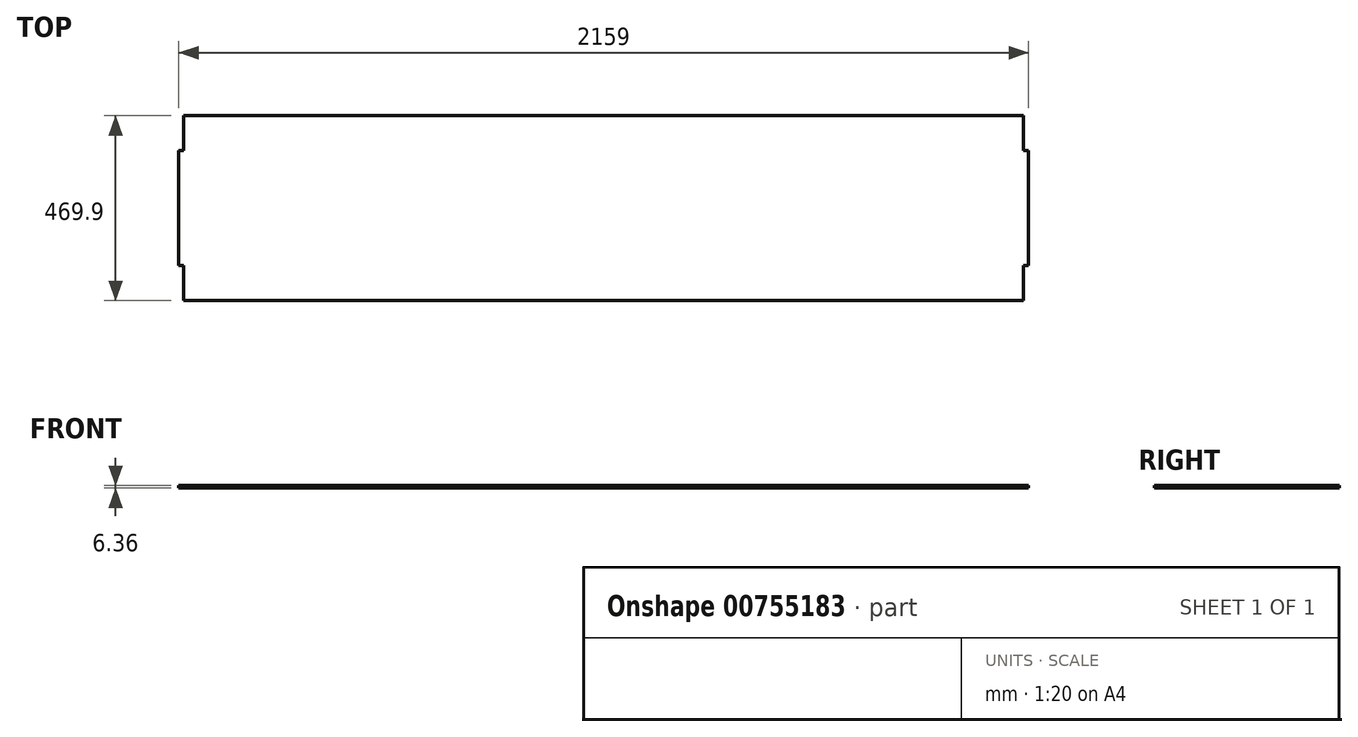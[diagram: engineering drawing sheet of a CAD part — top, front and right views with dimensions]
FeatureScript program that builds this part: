
annotation { "Feature Type Name" : "Feature", "Feature Type Description" : "" }
export const myFeature = defineFeature(function(context is Context, id is Id, definition is map)
    precondition{}
    {
        {
            var Q0;
            Q0=qCreatedBy(makeId("Top.planeOp"),FACE);
            var sketch = newSketch(context, id + "F0", { "sketchPlane" : qUnion([Q0])});
            skLineSegment(sketch, "E0.bottom", {"start": v(-1079.5, 234.95) * mm, "end": v(1079.5, 234.95) * mm});
            skLineSegment(sketch, "E0.top", {"start": v(-1079.5, -234.95) * mm, "end": v(1079.5, -234.95) * mm});
            skLineSegment(sketch, "E0.left", {"start": v(-1079.5, 234.95) * mm, "end": v(-1079.5, -234.95) * mm});
            skLineSegment(sketch, "E0.right", {"start": v(1079.5, 234.95) * mm, "end": v(1079.5, -234.95) * mm});
            skPoint(sketch, "E0.middle", {"position": v(0, 0) * mm});
            skSolve(sketch);
        }
        {
            var Q0;
            Q0 = qSketchRegion(id + "F0", true);
            extrude(context, id + "F1", {"entities" : qUnion([Q0]), "endBound" : BoundingType.SYMMETRIC, "depth" : 6.35 * mm, "offsetDistance" : 25.4 * mm});
        }
        {
            var Q0;
            Q0=makeQuery(id+"F1.opExtrude","CAP_FACE",FACE,{"disambiguationData":[OSD([sQuery(id+"F0.wireOp",EDGE,"E0.bottom"),sQuery(id+"F0.wireOp",EDGE,"E0.top"),sQuery(id+"F0.wireOp",EDGE,"E0.left"),sQuery(id+"F0.wireOp",EDGE,"E0.right")])],"isStart":false});
            var sketch = newSketch(context, id + "F2", { "sketchPlane" : qUnion([Q0])});
            skLineSegment(sketch, "E1", {"start": v(-1079.5, 0) * mm, "end": v(1079.5, 0) * mm, "construction": true});
            skLineSegment(sketch, "E2.bottom", {"start": v(-1079.5, 234.95) * mm, "end": v(-1066.8, 234.95) * mm});
            skLineSegment(sketch, "E2.top", {"start": v(-1079.5, 146.05) * mm, "end": v(-1066.8, 146.05) * mm});
            skLineSegment(sketch, "E2.left", {"start": v(-1079.5, 234.95) * mm, "end": v(-1079.5, 146.05) * mm});
            skLineSegment(sketch, "E2.right", {"start": v(-1066.8, 234.95) * mm, "end": v(-1066.8, 146.05) * mm});
            skLineSegment(sketch, "E3", {"start": v(0, -234.95) * mm, "end": v(0, 234.95) * mm, "construction": true});
            skLineSegment(sketch, "E4.MirrorCS", {"start": v(-1079.5, -234.95) * mm, "end": v(-1066.8, -234.95) * mm});
            skLineSegment(sketch, "E5.MirrorCS", {"start": v(-1079.5, -146.05) * mm, "end": v(-1066.8, -146.05) * mm});
            skLineSegment(sketch, "E6.MirrorCS", {"start": v(-1079.5, -234.95) * mm, "end": v(-1079.5, -146.05) * mm});
            skLineSegment(sketch, "E7.MirrorCS", {"start": v(-1066.8, -234.95) * mm, "end": v(-1066.8, -146.05) * mm});
            skLineSegment(sketch, "E8.MirrorCS", {"start": v(1079.5, 146.05) * mm, "end": v(1066.8, 146.05) * mm});
            skLineSegment(sketch, "E9.MirrorCS", {"start": v(1079.5, -146.05) * mm, "end": v(1066.8, -146.05) * mm});
            skLineSegment(sketch, "E10.MirrorCS", {"start": v(1079.5, 234.95) * mm, "end": v(1066.8, 234.95) * mm});
            skLineSegment(sketch, "E11.MirrorCS", {"start": v(1079.5, -234.95) * mm, "end": v(1066.8, -234.95) * mm});
            skLineSegment(sketch, "E12.MirrorCS", {"start": v(1079.5, -234.95) * mm, "end": v(1079.5, -146.05) * mm});
            skLineSegment(sketch, "E13.MirrorCS", {"start": v(1066.8, -234.95) * mm, "end": v(1066.8, -146.05) * mm});
            skLineSegment(sketch, "E14.MirrorCS", {"start": v(1066.8, 234.95) * mm, "end": v(1066.8, 146.05) * mm});
            skLineSegment(sketch, "E15.MirrorCS", {"start": v(1079.5, 234.95) * mm, "end": v(1079.5, 146.05) * mm});
            skSolve(sketch);
        }
        {
            var Q0;
            Q0 = qSketchRegion(id + "F2", true);
            extrude(context, id + "F3", {"entities" : qUnion([Q0]), "operationType" : NewBodyOperationType.REMOVE, "endBound" : BoundingType.THROUGH_ALL, "oppositeDirection" : true, "depth" : 25.4 * mm, "offsetDistance" : 25.4 * mm});
        }
    });
